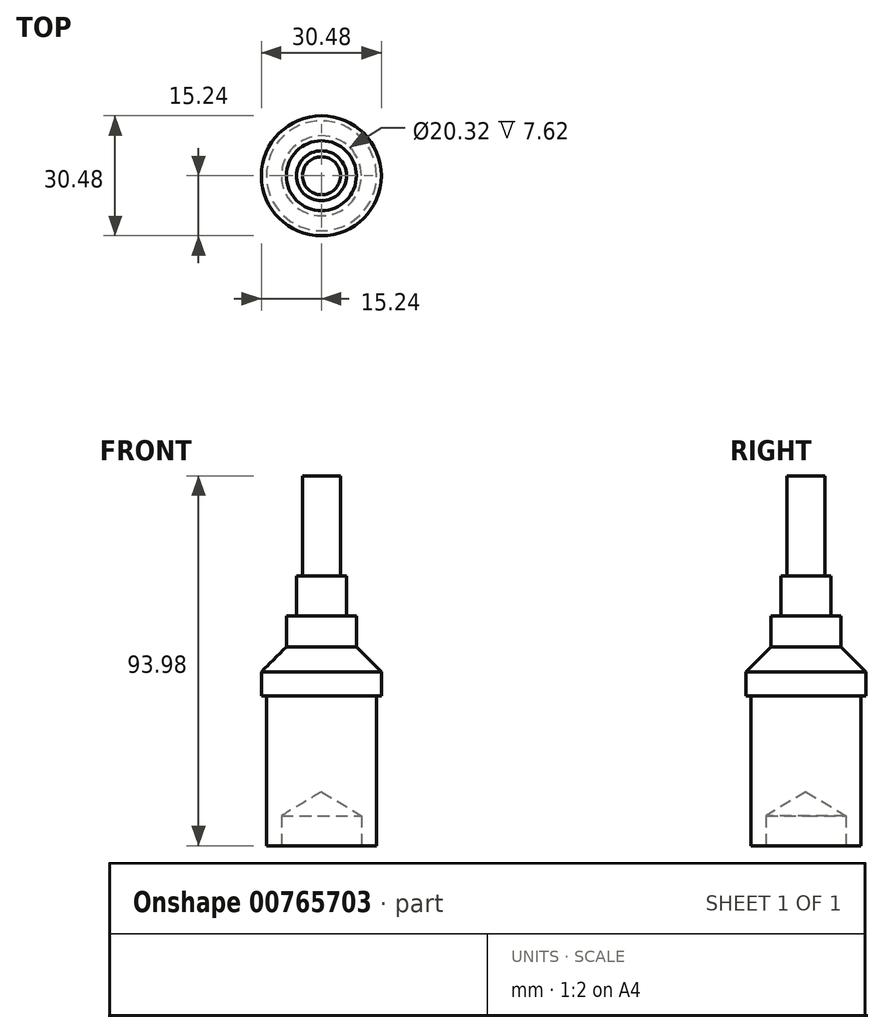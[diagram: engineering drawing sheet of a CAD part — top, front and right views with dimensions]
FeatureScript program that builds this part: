
annotation { "Feature Type Name" : "Feature", "Feature Type Description" : "" }
export const myFeature = defineFeature(function(context is Context, id is Id, definition is map)
    precondition{}
    {
        {
            var Q0;
            Q0=qCreatedBy(makeId("Top.planeOp"),FACE);
            var sketch = newSketch(context, id + "F0", { "sketchPlane" : qUnion([Q0])});
            skCircle(sketch, "E0", {"center": v(0, 0) * mm, "radius": 13.97 * mm});
            skSolve(sketch);
        }
        {
            var Q0;
            Q0 = qSketchRegion(id + "F0", true);
            extrude(context, id + "F1", {"entities" : qUnion([Q0]), "depth" : 38.1 * mm, "offsetDistance" : 25.4 * mm});
        }
        {
            var Q0;
            Q0=makeQuery(id+"F1.opExtrude","CAP_FACE",FACE,{"disambiguationData":[OSD([sQuery(id+"F0.wireOp",EDGE,"E0")])],"isStart":false});
            var sketch = newSketch(context, id + "F2", { "sketchPlane" : qUnion([Q0])});
            skCircle(sketch, "E1", {"center": v(0, 0) * mm, "radius": 15.24 * mm});
            skSolve(sketch);
        }
        {
            var Q0;
            Q0 = qSketchRegion(id + "F2", true);
            extrude(context, id + "F3", {"entities" : qUnion([Q0]), "operationType" : NewBodyOperationType.ADD, "depth" : 12.7 * mm, "offsetDistance" : 25.4 * mm});
        }
        {
            var Q0;
            Q0=makeQuery(id+"F3.opExtrude","CAP_FACE",FACE,{"disambiguationData":[OSD([sQuery(id+"F2.wireOp",EDGE,"E1")])],"isStart":false});
            var sketch = newSketch(context, id + "F4", { "sketchPlane" : qUnion([Q0])});
            skCircle(sketch, "E2", {"center": v(0, 0) * mm, "radius": 8.9 * mm});
            skSolve(sketch);
        }
        {
            var Q0;
            Q0 = qSketchRegion(id + "F4", true);
            extrude(context, id + "F5", {"entities" : qUnion([Q0]), "operationType" : NewBodyOperationType.ADD, "depth" : 7.62 * mm, "offsetDistance" : 25.4 * mm});
        }
        {
            var Q0;
            Q0=makeQuery(id+"F5.opExtrude","CAP_FACE",FACE,{"disambiguationData":[OSD([sQuery(id+"F4.wireOp",EDGE,"E2")])],"isStart":false});
            var sketch = newSketch(context, id + "F6", { "sketchPlane" : qUnion([Q0])});
            skCircle(sketch, "E3", {"center": v(0, 0) * mm, "radius": 6.35 * mm});
            skSolve(sketch);
        }
        {
            var Q0;
            Q0 = qSketchRegion(id + "F6", true);
            extrude(context, id + "F7", {"entities" : qUnion([Q0]), "operationType" : NewBodyOperationType.ADD, "depth" : 10.16 * mm, "offsetDistance" : 25.4 * mm});
        }
        {
            var Q0;
            Q0=makeQuery(id+"F7.opExtrude","CAP_FACE",FACE,{"disambiguationData":[OSD([sQuery(id+"F6.wireOp",EDGE,"E3")])],"isStart":false});
            var sketch = newSketch(context, id + "F8", { "sketchPlane" : qUnion([Q0])});
            skCircle(sketch, "E4", {"center": v(0, 0) * mm, "radius": 4.83 * mm});
            skSolve(sketch);
        }
        {
            var Q0;
            Q0 = qSketchRegion(id + "F8", true);
            extrude(context, id + "F9", {"entities" : qUnion([Q0]), "operationType" : NewBodyOperationType.ADD, "depth" : 25.4 * mm, "offsetDistance" : 25.4 * mm});
        }
        {
            var Q0;
            Q0=makeQuery(id+"F3.opExtrude","CAP_EDGE",EDGE,{"disambiguationData":[OSD([sQuery(id+"F2.wireOp",EDGE,"E1")])],"isStart":false});
            chamfer(context, id + "F10", {"entities" : qUnion([Q0]), "chamferType" : ChamferType.OFFSET_ANGLE, "width" : 6.6 * mm, "oppositeDirection" : false, "angle" : 45 * degree, "tangentPropagation" : true});
        }
        {
            var Q0;
            Q0=makeQuery(id+"F1.opExtrude","CAP_FACE",FACE,{"disambiguationData":[OSD([sQuery(id+"F0.wireOp",EDGE,"E0")])],"isStart":true});
            var sketch = newSketch(context, id + "F11", { "sketchPlane" : qUnion([Q0])});
            skCircle(sketch, "E5", {"center": v(0, 0) * mm, "radius": 10.16 * mm});
            skSolve(sketch);
        }
        {
            var Q0;
            Q0=sQuery(id+"F11.wireOp",VERTEX,"E5.center");
            var Q1;
            Q1=makeQuery(id+"F1.opExtrude","SWEPT_BODY",BODY,{"disambiguationData":[OSD([sQuery(id+"F0.wireOp",EDGE,"E0")])]});
            hole(context, id + "F12", {"style" : HoleStyle.SIMPLE, "endStyle" : HoleEndStyle.BLIND, "holeDiameter" : 20.32 * mm, "majorDiameter" : 6.35 * mm, "holeDepth" : 7.62 * mm, "isTappedThrough" : true, "tappedDepth" : 12.7 * mm, "tapClearance" : 3, "locations" : qUnion([Q0]), "scope" : qUnion([Q1])});
        }
    });
